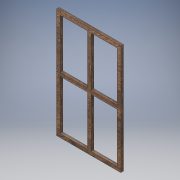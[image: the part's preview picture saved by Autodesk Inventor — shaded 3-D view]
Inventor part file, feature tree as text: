
AUTODESK INVENTOR PART (.ipt)
format: ipt  version: 2017 (Build 210142000, 142)  size: 138,240 bytes
history: native  units: in
note: dims shown in document units (in); Inventor stores cm internally (conversion verified against a paired STEP export)
features: extrude x2, sketch x2, projected_geometry x1
ambient origin geometry x8: Origin, YZ Plane, XZ Plane, XY Plane, X Axis, Y Axis, Z Axis, Center Point
bodies: Solid1 (feature_tree)
feature tree (5):
  extrude  "Extrusion1"  Depth=30.75in
  extrude  "Extrusion2"  Depth=0.75in TaperAngle=0.0deg
  sketch  "Sketch1"  dims[d0=18.0in d1=30.75in]
  sketch  "Sketch2"  dims[d2=0.75in d3=0.0in d22=0.75in d23=0.0in d24=1.0in d25=1.0in d26=1.0in d27=1.0in d28=1.0in d29=1.0in d30=1.0in d31=1.0in d32=1.0in d33=1.0in d34=7.3125in d35=7.6875in d36=13.875in]
  projected_geometry  "Projected Loop1"
